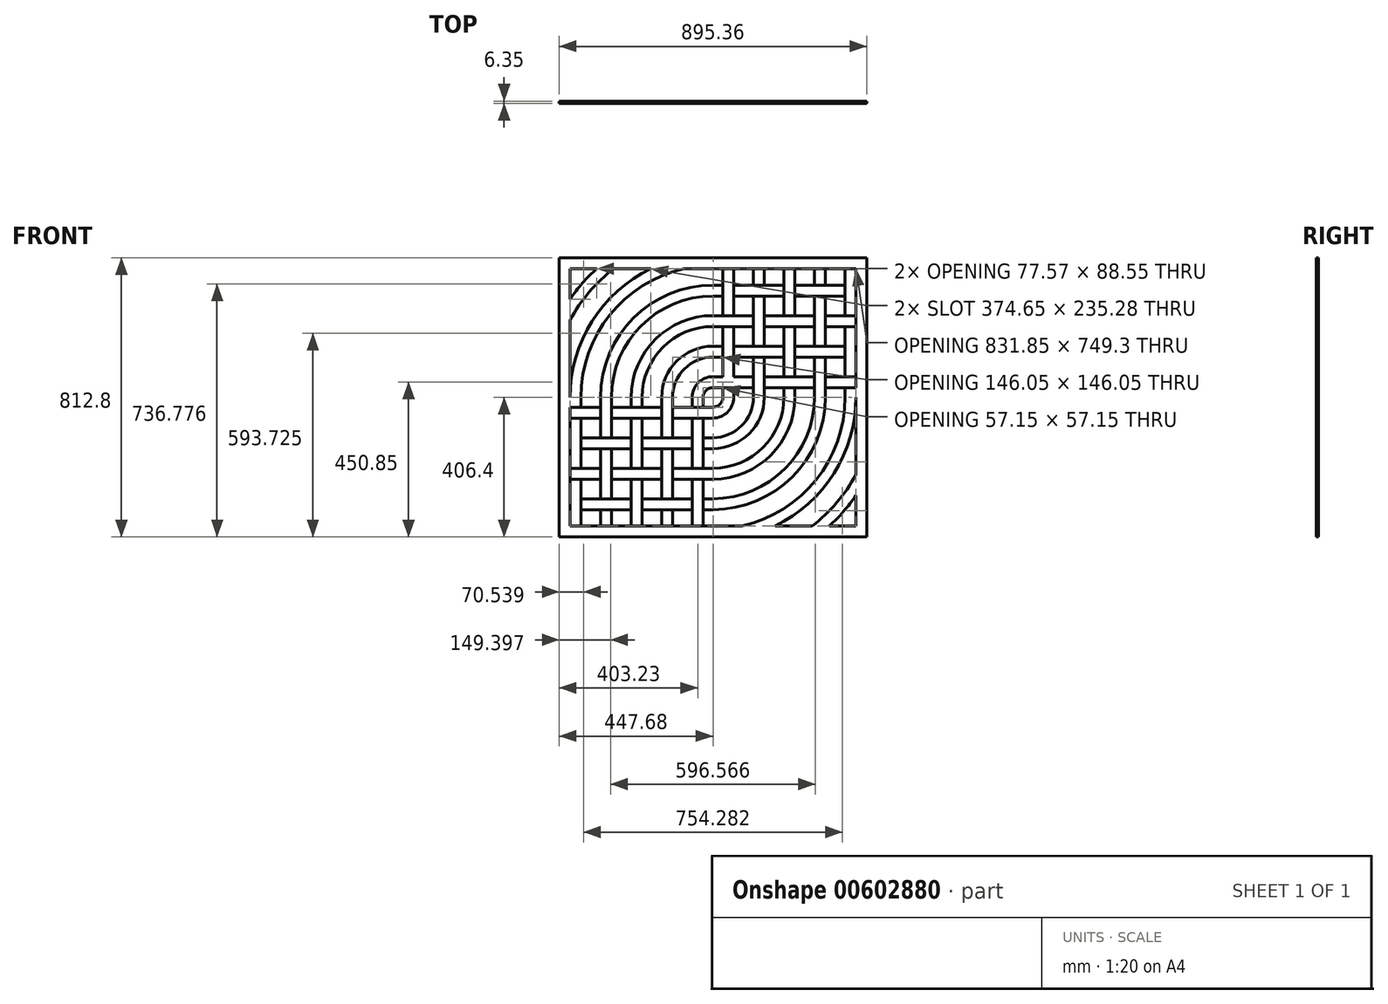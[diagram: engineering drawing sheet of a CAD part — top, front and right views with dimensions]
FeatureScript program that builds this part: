
annotation { "Feature Type Name" : "Feature", "Feature Type Description" : "" }
export const myFeature = defineFeature(function(context is Context, id is Id, definition is map)
    precondition{}
    {
        {
            var Q0;
            Q0=qCreatedBy(makeId("Front.planeOp"),FACE);
            var sketch = newSketch(context, id + "F0", { "sketchPlane" : qUnion([Q0])});
            skLineSegment(sketch, "E0.bottom", {"start": v(447.67, -406.4) * mm, "end": v(-447.68, -406.4) * mm});
            skLineSegment(sketch, "E0.top", {"start": v(447.68, 406.4) * mm, "end": v(-447.68, 406.4) * mm});
            skPoint(sketch, "E0.middle", {"position": v(0, 0) * mm});
            skArc(sketch, "E1", {"start": v(0, 28.58) * mm, "mid": v(-20.2, 20.2) * mm, "end": v(-28.58, 0) * mm});
            skArc(sketch, "E2.0", {"start": v(0, 60.33) * mm, "mid": v(-42.66, 42.66) * mm, "end": v(-60.33, 0) * mm});
            skLineSegment(sketch, "E3.0", {"start": v(415.93, 374.65) * mm, "end": v(-415.92, 374.65) * mm});
            skLineSegment(sketch, "E4.0", {"start": v(415.93, -374.65) * mm, "end": v(-415.93, -374.65) * mm});
            skArc(sketch, "E5.0", {"start": v(0, 117.48) * mm, "mid": v(-83.07, 83.07) * mm, "end": v(-117.48, 0) * mm});
            skArc(sketch, "E6.0", {"start": v(0, 149.22) * mm, "mid": v(-105.52, 105.52) * mm, "end": v(-149.22, 0) * mm});
            skArc(sketch, "E7.0", {"start": v(0, 206.38) * mm, "mid": v(-145.93, 145.93) * mm, "end": v(-206.38, 0) * mm});
            skLineSegment(sketch, "E8", {"start": v(-327.03, 0) * mm, "end": v(-327.03, -117.48) * mm});
            skLineSegment(sketch, "E9.0", {"start": v(-295.28, 0) * mm, "end": v(-295.28, -117.48) * mm});
            skLineSegment(sketch, "E10.0", {"start": v(-238.13, 0) * mm, "end": v(-238.13, -28.58) * mm});
            skLineSegment(sketch, "E11.0", {"start": v(28.57, 0) * mm, "end": v(28.57, 28.57) * mm});
            skLineSegment(sketch, "E12.0", {"start": v(60.32, 0) * mm, "end": v(60.32, 28.57) * mm});
            skLineSegment(sketch, "E13.0", {"start": v(117.47, 0) * mm, "end": v(117.47, 117.48) * mm});
            skLineSegment(sketch, "E14.0", {"start": v(149.22, 0) * mm, "end": v(149.22, 117.48) * mm});
            skLineSegment(sketch, "E15.0", {"start": v(206.37, 0) * mm, "end": v(206.37, 28.58) * mm});
            skLineSegment(sketch, "E16.0", {"start": v(238.12, 0) * mm, "end": v(238.12, 28.58) * mm});
            skLineSegment(sketch, "E17.0", {"start": v(295.27, 0) * mm, "end": v(295.27, 117.48) * mm});
            skLineSegment(sketch, "E18.0", {"start": v(327.02, 0) * mm, "end": v(327.02, 117.48) * mm});
            skLineSegment(sketch, "E19.0", {"start": v(-28.58, 0) * mm, "end": v(-28.58, -28.58) * mm});
            skLineSegment(sketch, "E20.0", {"start": v(-60.33, 0) * mm, "end": v(-60.33, -28.58) * mm});
            skLineSegment(sketch, "E21.0", {"start": v(-117.48, 0) * mm, "end": v(-117.48, -117.48) * mm});
            skLineSegment(sketch, "E22.0", {"start": v(-149.23, 0) * mm, "end": v(-149.23, -117.48) * mm});
            skLineSegment(sketch, "E23.0", {"start": v(-206.38, 0) * mm, "end": v(-206.38, -28.58) * mm});
            skLineSegment(sketch, "E24", {"start": v(0, 28.58) * mm, "end": v(117.47, 28.58) * mm});
            skLineSegment(sketch, "E25", {"start": v(0, 60.33) * mm, "end": v(117.47, 60.33) * mm});
            skLineSegment(sketch, "E26", {"start": v(0, -28.58) * mm, "end": v(-117.48, -28.58) * mm});
            skLineSegment(sketch, "E27", {"start": v(0, -60.33) * mm, "end": v(-117.48, -60.33) * mm});
            skLineSegment(sketch, "E28.0", {"start": v(0, 117.48) * mm, "end": v(28.57, 117.48) * mm});
            skLineSegment(sketch, "E29", {"start": v(0, 149.22) * mm, "end": v(28.57, 149.22) * mm});
            skLineSegment(sketch, "E30", {"start": v(0, 206.38) * mm, "end": v(118.8, 206.38) * mm});
            skLineSegment(sketch, "E31", {"start": v(0, 238.12) * mm, "end": v(117.47, 238.12) * mm});
            skLineSegment(sketch, "E32", {"start": v(0, 295.28) * mm, "end": v(28.57, 295.28) * mm});
            skLineSegment(sketch, "E33", {"start": v(0, 327.03) * mm, "end": v(28.57, 327.03) * mm});
            skArc(sketch, "E34.0", {"start": v(-85.02, 374.65) * mm, "mid": v(-300.2, 239.72) * mm, "end": v(-384.18, 0) * mm});
            skArc(sketch, "E35.0", {"start": v(-288.86, 374.65) * mm, "mid": v(-360.2, 306.68) * mm, "end": v(-415.93, 225.4) * mm});
            skArc(sketch, "E36.0", {"start": v(-338.36, 374.65) * mm, "mid": v(-379.73, 332.64) * mm, "end": v(-415.92, 286.1) * mm});
            skArc(sketch, "E37.trimOffspring", {"start": v(384.58, 327.02) * mm, "mid": v(384.38, 327.26) * mm, "end": v(384.17, 327.5) * mm});
            skArc(sketch, "E38.trimOffspring", {"start": v(338.36, -374.65) * mm, "mid": v(379.73, -332.64) * mm, "end": v(415.93, -286.1) * mm});
            skArc(sketch, "E39.trimOffspring", {"start": v(288.86, -374.65) * mm, "mid": v(360.2, -306.68) * mm, "end": v(415.93, -225.4) * mm});
            skArc(sketch, "E40.trimOffspring", {"start": v(180.64, -374.65) * mm, "mid": v(352.23, -221.2) * mm, "end": v(415.93, 0) * mm});
            skArc(sketch, "E41.trimOffspring", {"start": v(85.02, -374.65) * mm, "mid": v(300.2, -239.72) * mm, "end": v(384.18, 0) * mm});
            skLineSegment(sketch, "E42", {"start": v(-415.93, 0) * mm, "end": v(-415.93, 374.65) * mm});
            skLineSegment(sketch, "E43", {"start": v(-415.93, 0) * mm, "end": v(-415.93, -374.65) * mm});
            skLineSegment(sketch, "E44", {"start": v(415.93, 0) * mm, "end": v(415.93, 374.65) * mm});
            skLineSegment(sketch, "E45", {"start": v(415.93, 0) * mm, "end": v(415.93, -374.65) * mm});
            skLineSegment(sketch, "E46.0", {"start": v(-447.68, 0) * mm, "end": v(-447.68, 406.4) * mm});
            skLineSegment(sketch, "E47.0", {"start": v(447.68, 0) * mm, "end": v(447.68, -406.4) * mm});
            skLineSegment(sketch, "E48.0", {"start": v(447.68, 0) * mm, "end": v(447.68, 406.4) * mm});
            skLineSegment(sketch, "E49", {"start": v(-447.68, 0) * mm, "end": v(-447.68, -406.4) * mm});
            skLineSegment(sketch, "E50", {"start": v(0, -117.48) * mm, "end": v(-28.58, -117.48) * mm});
            skLineSegment(sketch, "E51", {"start": v(0, -149.22) * mm, "end": v(-28.58, -149.22) * mm});
            skLineSegment(sketch, "E52", {"start": v(0, -206.38) * mm, "end": v(-118.8, -206.38) * mm});
            skLineSegment(sketch, "E53", {"start": v(0, -238.12) * mm, "end": v(-117.48, -238.12) * mm});
            skLineSegment(sketch, "E54", {"start": v(0, -295.28) * mm, "end": v(-28.58, -295.28) * mm});
            skLineSegment(sketch, "E55", {"start": v(0, -327.03) * mm, "end": v(-28.58, -327.03) * mm});
            skLineSegment(sketch, "E56.0", {"start": v(384.18, 0) * mm, "end": v(384.18, 28.58) * mm});
            skArc(sketch, "E57.trimOffspring", {"start": v(118.8, 206.38) * mm, "mid": v(118.14, 206.75) * mm, "end": v(117.47, 207.13) * mm});
            skArc(sketch, "E58.trimOffspring", {"start": v(0, 238.12) * mm, "mid": v(-168.38, 168.38) * mm, "end": v(-238.12, 0) * mm});
            skPoint(sketch, "E59.orphan", {"position": v(0, 238.12) * mm});
            skPoint(sketch, "E60.orphan", {"position": v(0, 206.38) * mm});
            skArc(sketch, "E61.trimOffspring", {"start": v(0, 295.28) * mm, "mid": v(-208.8, 208.8) * mm, "end": v(-295.28, 0) * mm});
            skArc(sketch, "E62.trimOffspring", {"start": v(0, 327.03) * mm, "mid": v(-231.24, 231.24) * mm, "end": v(-327.03, 0) * mm});
            skLineSegment(sketch, "E63.0", {"start": v(-384.18, 0) * mm, "end": v(-384.18, -28.58) * mm});
            skArc(sketch, "E64.trimOffspring", {"start": v(0, -28.58) * mm, "mid": v(20.2, -20.2) * mm, "end": v(28.58, 0) * mm});
            skArc(sketch, "E65.trimOffspring", {"start": v(0, -60.33) * mm, "mid": v(42.66, -42.66) * mm, "end": v(60.33, 0) * mm});
            skArc(sketch, "E66.trimOffspring", {"start": v(0, -117.48) * mm, "mid": v(83.07, -83.07) * mm, "end": v(117.48, 0) * mm});
            skArc(sketch, "E67.trimOffspring", {"start": v(0, -149.22) * mm, "mid": v(105.52, -105.52) * mm, "end": v(149.22, 0) * mm});
            skArc(sketch, "E68.trimOffspring", {"start": v(0, -206.38) * mm, "mid": v(145.93, -145.93) * mm, "end": v(206.38, 0) * mm});
            skArc(sketch, "E69.trimOffspring", {"start": v(0, -238.12) * mm, "mid": v(168.38, -168.38) * mm, "end": v(238.12, 0) * mm});
            skArc(sketch, "E70.trimOffspring", {"start": v(0, -295.28) * mm, "mid": v(208.8, -208.8) * mm, "end": v(295.28, 0) * mm});
            skArc(sketch, "E71.trimOffspring", {"start": v(0, -327.03) * mm, "mid": v(231.24, -231.24) * mm, "end": v(327.03, 0) * mm});
            skArc(sketch, "E72.trimOffspring", {"start": v(-118.8, -206.38) * mm, "mid": v(-118.14, -206.75) * mm, "end": v(-117.48, -207.13) * mm});
            skLineSegment(sketch, "E73.trimOffspring", {"start": v(-117.48, -207.13) * mm, "end": v(-117.48, -295.28) * mm});
            skArc(sketch, "E74.trimOffspring", {"start": v(-384.58, -327.03) * mm, "mid": v(-384.38, -327.26) * mm, "end": v(-384.18, -327.5) * mm});
            skArc(sketch, "E75.0", {"start": v(-180.64, 374.65) * mm, "mid": v(-352.23, 221.2) * mm, "end": v(-415.93, 0) * mm});
            skLineSegment(sketch, "E76.trimOffspring", {"start": v(28.57, 60.33) * mm, "end": v(28.57, 206.38) * mm});
            skLineSegment(sketch, "E77.trimOffspring", {"start": v(60.32, 60.33) * mm, "end": v(60.32, 206.38) * mm});
            skLineSegment(sketch, "E78.trimOffspring", {"start": v(149.22, 60.33) * mm, "end": v(295.27, 60.33) * mm});
            skLineSegment(sketch, "E79.trimOffspring", {"start": v(149.22, 28.58) * mm, "end": v(295.27, 28.58) * mm});
            skLineSegment(sketch, "E80.trimOffspring", {"start": v(206.37, 60.33) * mm, "end": v(206.37, 206.38) * mm});
            skLineSegment(sketch, "E81.trimOffspring", {"start": v(238.12, 60.33) * mm, "end": v(238.12, 206.38) * mm});
            skLineSegment(sketch, "E82.trimOffspring", {"start": v(327.02, 28.58) * mm, "end": v(415.93, 28.58) * mm});
            skLineSegment(sketch, "E83.trimOffspring", {"start": v(327.02, 60.33) * mm, "end": v(415.93, 60.33) * mm});
            skLineSegment(sketch, "E84.trimOffspring", {"start": v(384.18, 60.33) * mm, "end": v(384.18, 206.38) * mm});
            skLineSegment(sketch, "E85.trimOffspring", {"start": v(327.02, 149.22) * mm, "end": v(327.02, 295.28) * mm});
            skLineSegment(sketch, "E86.trimOffspring", {"start": v(295.27, 149.22) * mm, "end": v(295.27, 295.28) * mm});
            skLineSegment(sketch, "E87.trimOffspring", {"start": v(117.47, 149.22) * mm, "end": v(117.47, 295.28) * mm});
            skLineSegment(sketch, "E88.trimOffspring", {"start": v(149.22, 149.22) * mm, "end": v(149.22, 295.28) * mm});
            skLineSegment(sketch, "E89.trimOffspring", {"start": v(238.12, 149.22) * mm, "end": v(384.18, 149.22) * mm});
            skLineSegment(sketch, "E90.trimOffspring", {"start": v(238.12, 117.48) * mm, "end": v(384.18, 117.48) * mm});
            skLineSegment(sketch, "E91.trimOffspring", {"start": v(60.32, 117.48) * mm, "end": v(206.37, 117.48) * mm});
            skLineSegment(sketch, "E92.trimOffspring", {"start": v(60.32, 149.22) * mm, "end": v(206.37, 149.22) * mm});
            skLineSegment(sketch, "E93.trimOffspring", {"start": v(28.57, 238.12) * mm, "end": v(28.57, 374.65) * mm});
            skLineSegment(sketch, "E94.trimOffspring", {"start": v(60.32, 238.12) * mm, "end": v(60.32, 374.65) * mm});
            skLineSegment(sketch, "E95.trimOffspring", {"start": v(149.22, 238.12) * mm, "end": v(295.27, 238.12) * mm});
            skLineSegment(sketch, "E96.trimOffspring", {"start": v(149.22, 206.38) * mm, "end": v(295.27, 206.38) * mm});
            skLineSegment(sketch, "E97.trimOffspring", {"start": v(206.37, 238.12) * mm, "end": v(206.37, 374.65) * mm});
            skLineSegment(sketch, "E98.trimOffspring", {"start": v(238.12, 238.12) * mm, "end": v(238.12, 374.65) * mm});
            skLineSegment(sketch, "E99.trimOffspring", {"start": v(327.02, 238.12) * mm, "end": v(415.93, 238.12) * mm});
            skLineSegment(sketch, "E100.trimOffspring", {"start": v(327.02, 206.38) * mm, "end": v(415.93, 206.38) * mm});
            skLineSegment(sketch, "E101.trimOffspring", {"start": v(384.18, 238.12) * mm, "end": v(384.18, 374.65) * mm});
            skLineSegment(sketch, "E102.trimOffspring", {"start": v(327.02, 327.03) * mm, "end": v(327.02, 374.65) * mm});
            skLineSegment(sketch, "E103.trimOffspring", {"start": v(295.27, 327.03) * mm, "end": v(295.27, 374.65) * mm});
            skLineSegment(sketch, "E104.trimOffspring", {"start": v(238.12, 327.03) * mm, "end": v(384.58, 327.03) * mm});
            skLineSegment(sketch, "E105.trimOffspring", {"start": v(238.12, 295.28) * mm, "end": v(384.18, 295.28) * mm});
            skLineSegment(sketch, "E106.trimOffspring", {"start": v(149.22, 327.03) * mm, "end": v(149.22, 374.65) * mm});
            skLineSegment(sketch, "E107.trimOffspring", {"start": v(117.47, 327.03) * mm, "end": v(117.47, 374.65) * mm});
            skLineSegment(sketch, "E108.trimOffspring", {"start": v(60.32, 327.03) * mm, "end": v(206.37, 327.03) * mm});
            skLineSegment(sketch, "E109.trimOffspring", {"start": v(60.32, 295.28) * mm, "end": v(206.37, 295.28) * mm});
            skLineSegment(sketch, "E110.trimOffspring", {"start": v(-149.23, -28.58) * mm, "end": v(-295.28, -28.58) * mm});
            skLineSegment(sketch, "E111.trimOffspring", {"start": v(-149.23, -60.33) * mm, "end": v(-295.28, -60.33) * mm});
            skLineSegment(sketch, "E112.trimOffspring", {"start": v(-60.33, -60.32) * mm, "end": v(-60.33, -206.38) * mm});
            skLineSegment(sketch, "E113.trimOffspring", {"start": v(-28.58, -60.32) * mm, "end": v(-28.58, -206.38) * mm});
            skLineSegment(sketch, "E114.trimOffspring", {"start": v(-60.33, -117.48) * mm, "end": v(-206.38, -117.48) * mm});
            skLineSegment(sketch, "E115.trimOffspring", {"start": v(-60.33, -149.22) * mm, "end": v(-206.38, -149.22) * mm});
            skLineSegment(sketch, "E116.trimOffspring", {"start": v(-117.48, -149.22) * mm, "end": v(-117.48, -206.38) * mm});
            skLineSegment(sketch, "E117.trimOffspring", {"start": v(-149.23, -149.22) * mm, "end": v(-149.23, -295.28) * mm});
            skLineSegment(sketch, "E118.trimOffspring", {"start": v(-149.23, -206.38) * mm, "end": v(-295.28, -206.38) * mm});
            skLineSegment(sketch, "E119.trimOffspring", {"start": v(-149.23, -238.12) * mm, "end": v(-295.28, -238.12) * mm});
            skLineSegment(sketch, "E120.trimOffspring", {"start": v(-60.33, -238.12) * mm, "end": v(-60.33, -374.65) * mm});
            skLineSegment(sketch, "E121.trimOffspring", {"start": v(-28.58, -238.12) * mm, "end": v(-28.58, -374.65) * mm});
            skLineSegment(sketch, "E122.trimOffspring", {"start": v(-60.33, -295.28) * mm, "end": v(-206.38, -295.28) * mm});
            skLineSegment(sketch, "E123.trimOffspring", {"start": v(-60.33, -327.03) * mm, "end": v(-206.38, -327.03) * mm});
            skLineSegment(sketch, "E124.trimOffspring", {"start": v(-117.48, -327.03) * mm, "end": v(-117.48, -374.65) * mm});
            skLineSegment(sketch, "E125.trimOffspring", {"start": v(-149.23, -327.03) * mm, "end": v(-149.23, -374.65) * mm});
            skLineSegment(sketch, "E126.trimOffspring", {"start": v(-238.12, -327.03) * mm, "end": v(-384.58, -327.03) * mm});
            skLineSegment(sketch, "E127.trimOffspring", {"start": v(-238.12, -295.28) * mm, "end": v(-384.18, -295.28) * mm});
            skLineSegment(sketch, "E128.trimOffspring", {"start": v(-206.38, -238.12) * mm, "end": v(-206.38, -374.65) * mm});
            skLineSegment(sketch, "E129.trimOffspring", {"start": v(-238.12, -238.12) * mm, "end": v(-238.12, -374.65) * mm});
            skLineSegment(sketch, "E130.trimOffspring", {"start": v(-238.12, -149.22) * mm, "end": v(-384.18, -149.22) * mm});
            skLineSegment(sketch, "E131.trimOffspring", {"start": v(-238.12, -117.48) * mm, "end": v(-384.18, -117.48) * mm});
            skLineSegment(sketch, "E132.trimOffspring", {"start": v(-206.38, -60.32) * mm, "end": v(-206.38, -206.38) * mm});
            skLineSegment(sketch, "E133.trimOffspring", {"start": v(-238.13, -60.32) * mm, "end": v(-238.12, -206.38) * mm});
            skLineSegment(sketch, "E134.trimOffspring", {"start": v(-327.03, -60.33) * mm, "end": v(-419.1, -60.33) * mm});
            skLineSegment(sketch, "E135.trimOffspring", {"start": v(-327.03, -28.58) * mm, "end": v(-419.1, -28.58) * mm});
            skLineSegment(sketch, "E136.trimOffspring", {"start": v(-384.18, -60.33) * mm, "end": v(-384.18, -206.38) * mm});
            skPoint(sketch, "E137.orphan", {"position": v(-415.93, -117.48) * mm});
            skPoint(sketch, "E138.orphan", {"position": v(-415.93, -149.22) * mm});
            skLineSegment(sketch, "E139.trimOffspring", {"start": v(-327.03, -149.22) * mm, "end": v(-327.03, -295.28) * mm});
            skLineSegment(sketch, "E140.trimOffspring", {"start": v(-295.28, -149.22) * mm, "end": v(-295.28, -295.28) * mm});
            skLineSegment(sketch, "E141.trimOffspring", {"start": v(-327.03, -206.38) * mm, "end": v(-415.93, -206.38) * mm});
            skLineSegment(sketch, "E142.trimOffspring", {"start": v(-327.03, -238.12) * mm, "end": v(-415.93, -238.12) * mm});
            skLineSegment(sketch, "E143.trimOffspring", {"start": v(-384.18, -238.12) * mm, "end": v(-384.18, -374.65) * mm});
            skLineSegment(sketch, "E144.trimOffspring", {"start": v(-295.28, -327.03) * mm, "end": v(-295.28, -374.65) * mm});
            skLineSegment(sketch, "E145.trimOffspring", {"start": v(-327.03, -327.03) * mm, "end": v(-327.03, -374.65) * mm});
            skSolve(sketch);
        }
        {
            var Q0;
            Q0=makeQuery(id+"F0.imprint","IMPRINT",FACE,{"disambiguationData":[TD([[makeQuery(id+"F0.imprint","IMPRINT",EDGE,{"derivedFrom":sQuery(id+"F0.wireOp",EDGE,"E0.bottom")}),-1.0]])]});
            extrude(context, id + "F1", {"entities" : qUnion([Q0]), "depth" : 6.35 * mm, "offsetDistance" : 25.4 * mm});
        }
        {
            var Q0;
            {var subQ0=sQuery(id+"F0.wireOp",EDGE,"E35.0");Q0=makeQuery(id+"F0.imprint","IMPRINT",FACE,{"disambiguationData":[TD([[makeQuery(id+"F0.imprint","IMPRINT",EDGE,{"derivedFrom":subQ0}),-1.0]])]});}
            var Q1;
            {var subQ4=sQuery(id+"F0.wireOp",EDGE,"E34.0");Q1=makeQuery(id+"F0.imprint","IMPRINT",FACE,{"disambiguationData":[TD([[makeQuery(id+"F0.imprint","IMPRINT",EDGE,{"derivedFrom":subQ4}),-1.0]])]});}
            var Q2;
            {var subQ7=sQuery(id+"F0.wireOp",EDGE,"E32");Q2=makeQuery(id+"F0.imprint","IMPRINT",FACE,{"disambiguationData":[TD([[makeQuery(id+"F0.imprint","IMPRINT",EDGE,{"derivedFrom":subQ7}),1.0]])]});}
            var Q3;
            {var subQ11=sQuery(id+"F0.wireOp",EDGE,"E7.0");Q3=makeQuery(id+"F0.imprint","IMPRINT",FACE,{"disambiguationData":[TD([[makeQuery(id+"F0.imprint","IMPRINT",EDGE,{"derivedFrom":subQ11}),-1.0]])]});}
            var Q4;
            {var subQ12=sQuery(id+"F0.wireOp",EDGE,"E5.0");Q4=makeQuery(id+"F0.imprint","IMPRINT",FACE,{"disambiguationData":[TD([[makeQuery(id+"F0.imprint","IMPRINT",EDGE,{"derivedFrom":subQ12}),-1.0]])]});}
            var Q5;
            {var subQ3=sQuery(id+"F0.wireOp",EDGE,"E1");Q5=makeQuery(id+"F0.imprint","IMPRINT",FACE,{"disambiguationData":[TD([[makeQuery(id+"F0.imprint","IMPRINT",EDGE,{"derivedFrom":subQ3}),-1.0]])]});}
            var Q6;
            {var subQ10=sQuery(id+"F0.wireOp",EDGE,"E11.0");Q6=makeQuery(id+"F0.imprint","IMPRINT",FACE,{"disambiguationData":[TD([[makeQuery(id+"F0.imprint","IMPRINT",EDGE,{"derivedFrom":subQ10}),-1.0]])]});}
            var Q7;
            {var subQ6=sQuery(id+"F0.wireOp",EDGE,"E50");Q7=makeQuery(id+"F0.imprint","IMPRINT",FACE,{"disambiguationData":[TD([[makeQuery(id+"F0.imprint","IMPRINT",EDGE,{"derivedFrom":subQ6}),1.0]])]});}
            var Q8;
            {var subQ10=sQuery(id+"F0.wireOp",EDGE,"E15.0");Q8=makeQuery(id+"F0.imprint","IMPRINT",FACE,{"disambiguationData":[TD([[makeQuery(id+"F0.imprint","IMPRINT",EDGE,{"derivedFrom":subQ10}),-1.0]])]});}
            var Q9;
            {var subQ1=sQuery(id+"F0.wireOp",EDGE,"E54");Q9=makeQuery(id+"F0.imprint","IMPRINT",FACE,{"disambiguationData":[TD([[makeQuery(id+"F0.imprint","IMPRINT",EDGE,{"derivedFrom":subQ1}),1.0]])]});}
            var Q10;
            {var subQ2=sQuery(id+"F0.wireOp",EDGE,"E40.trimOffspring");Q10=makeQuery(id+"F0.imprint","IMPRINT",FACE,{"disambiguationData":[TD([[makeQuery(id+"F0.imprint","IMPRINT",EDGE,{"derivedFrom":subQ2}),1.0]])]});}
            var Q11;
            {var subQ0=sQuery(id+"F0.wireOp",EDGE,"E38.trimOffspring");Q11=makeQuery(id+"F0.imprint","IMPRINT",FACE,{"disambiguationData":[TD([[makeQuery(id+"F0.imprint","IMPRINT",EDGE,{"derivedFrom":subQ0}),1.0]])]});}
            extrude(context, id + "F2", {"entities" : qUnion([Q0, Q1, Q2, Q3, Q4, Q5, Q6, Q7, Q8, Q9, Q10, Q11]), "operationType" : NewBodyOperationType.ADD, "depth" : 6.35 * mm, "offsetDistance" : 25.4 * mm});
        }
        {
            var Q0;
            {var subQ0=sQuery(id+"F0.wireOp",EDGE,"E134.trimOffspring");var subQ4=sQuery(id+"F0.wireOp",EDGE,"E8");var subQ5=makeQuery(id+"F0.imprint","INTERSECT",VERTEX,{"derivedFrom":[subQ4,subQ0]});Q0=makeQuery(id+"F0.imprint","IMPRINT",FACE,{"disambiguationData":[TD([[makeQuery(id+"F0.imprint","IMPRINT",EDGE,{"disambiguationData":[TD([[subQ5,1.0]])],"derivedFrom":subQ4}),-1.0]])]});}
            var Q1;
            {var subQ0=sQuery(id+"F0.wireOp",EDGE,"E110.trimOffspring");var subQ7=sQuery(id+"F0.wireOp",EDGE,"E9.0");var subQ8=makeQuery(id+"F0.imprint","INTERSECT",VERTEX,{"derivedFrom":[subQ7,subQ0]});Q1=makeQuery(id+"F0.imprint","IMPRINT",FACE,{"disambiguationData":[TD([[makeQuery(id+"F0.imprint","IMPRINT",EDGE,{"disambiguationData":[TD([[subQ8,-1.0]])],"derivedFrom":subQ7}),1.0]])]});}
            var Q2;
            {var subQ2=sQuery(id+"F0.wireOp",EDGE,"E133.trimOffspring");var subQ5=sQuery(id+"F0.wireOp",EDGE,"E130.trimOffspring");var subQ9=makeQuery(id+"F0.imprint","INTERSECT",VERTEX,{"derivedFrom":[subQ5,subQ2]});Q2=makeQuery(id+"F0.imprint","IMPRINT",FACE,{"disambiguationData":[TD([[makeQuery(id+"F0.imprint","IMPRINT",EDGE,{"disambiguationData":[TD([[subQ9,-1.0]])],"derivedFrom":subQ5}),-1.0]])]});}
            var Q3;
            {var subQ0=sQuery(id+"F0.wireOp",EDGE,"E114.trimOffspring");var subQ5=sQuery(id+"F0.wireOp",EDGE,"E112.trimOffspring");var subQ6=makeQuery(id+"F0.imprint","INTERSECT",VERTEX,{"derivedFrom":[subQ5,subQ0]});Q3=makeQuery(id+"F0.imprint","IMPRINT",FACE,{"disambiguationData":[TD([[makeQuery(id+"F0.imprint","IMPRINT",EDGE,{"disambiguationData":[TD([[subQ6,-1.0]])],"derivedFrom":subQ5}),-1.0]])]});}
            var Q4;
            {var subQ0=sQuery(id+"F0.wireOp",EDGE,"E141.trimOffspring");var subQ2=sQuery(id+"F0.wireOp",EDGE,"E43");var subQ3=makeQuery(id+"F0.imprint","INTERSECT",VERTEX,{"derivedFrom":[subQ2,subQ0]});Q4=makeQuery(id+"F0.imprint","IMPRINT",FACE,{"disambiguationData":[TD([[makeQuery(id+"F0.imprint","IMPRINT",EDGE,{"disambiguationData":[TD([[subQ3,-1.0]])],"derivedFrom":subQ2}),1.0]])]});}
            var Q5;
            {var subQ1=sQuery(id+"F0.wireOp",EDGE,"E118.trimOffspring");var subQ7=sQuery(id+"F0.wireOp",EDGE,"E117.trimOffspring");var subQ8=makeQuery(id+"F0.imprint","INTERSECT",VERTEX,{"derivedFrom":[subQ7,subQ1]});Q5=makeQuery(id+"F0.imprint","IMPRINT",FACE,{"disambiguationData":[TD([[makeQuery(id+"F0.imprint","IMPRINT",EDGE,{"disambiguationData":[TD([[subQ8,-1.0]])],"derivedFrom":subQ7}),-1.0]])]});}
            var Q6;
            {var subQ0=sQuery(id+"F0.wireOp",EDGE,"E129.trimOffspring");var subQ4=sQuery(id+"F0.wireOp",EDGE,"E126.trimOffspring");var subQ9=makeQuery(id+"F0.imprint","INTERSECT",VERTEX,{"derivedFrom":[subQ4,subQ0]});Q6=makeQuery(id+"F0.imprint","IMPRINT",FACE,{"disambiguationData":[TD([[makeQuery(id+"F0.imprint","IMPRINT",EDGE,{"disambiguationData":[TD([[subQ9,-1.0]])],"derivedFrom":subQ4}),-1.0]])]});}
            var Q7;
            {var subQ0=sQuery(id+"F0.wireOp",EDGE,"E122.trimOffspring");var subQ5=sQuery(id+"F0.wireOp",EDGE,"E120.trimOffspring");var subQ6=makeQuery(id+"F0.imprint","INTERSECT",VERTEX,{"derivedFrom":[subQ5,subQ0]});Q7=makeQuery(id+"F0.imprint","IMPRINT",FACE,{"disambiguationData":[TD([[makeQuery(id+"F0.imprint","IMPRINT",EDGE,{"disambiguationData":[TD([[subQ6,-1.0]])],"derivedFrom":subQ5}),-1.0]])]});}
            extrude(context, id + "F3", {"entities" : qUnion([Q0, Q1, Q2, Q3, Q4, Q5, Q6, Q7]), "depth" : 6.35 * mm, "offsetDistance" : 25.4 * mm});
        }
        {
            var Q0;
            {var subQ4=sQuery(id+"F0.wireOp",EDGE,"E141.trimOffspring");var subQ5=sQuery(id+"F0.wireOp",EDGE,"E43");var subQ6=makeQuery(id+"F0.imprint","INTERSECT",VERTEX,{"derivedFrom":[subQ5,subQ4]});Q0=makeQuery(id+"F0.imprint","IMPRINT",FACE,{"disambiguationData":[TD([[makeQuery(id+"F0.imprint","IMPRINT",EDGE,{"disambiguationData":[TD([[subQ6,1.0]])],"derivedFrom":subQ5}),1.0]])]});}
            var Q1;
            {var subQ0=sQuery(id+"F0.wireOp",EDGE,"E139.trimOffspring");var subQ9=sQuery(id+"F0.wireOp",EDGE,"E127.trimOffspring");var subQ10=makeQuery(id+"F0.imprint","INTERSECT",VERTEX,{"derivedFrom":[subQ9,subQ0]});Q1=makeQuery(id+"F0.imprint","IMPRINT",FACE,{"disambiguationData":[TD([[makeQuery(id+"F0.imprint","IMPRINT",EDGE,{"disambiguationData":[TD([[subQ10,1.0]])],"derivedFrom":subQ9}),-1.0]])]});}
            var Q2;
            {var subQ0=sQuery(id+"F0.wireOp",EDGE,"E132.trimOffspring");var subQ3=sQuery(id+"F0.wireOp",EDGE,"E111.trimOffspring");var subQ4=makeQuery(id+"F0.imprint","INTERSECT",VERTEX,{"derivedFrom":[subQ3,subQ0]});Q2=makeQuery(id+"F0.imprint","IMPRINT",FACE,{"disambiguationData":[TD([[makeQuery(id+"F0.imprint","IMPRINT",EDGE,{"disambiguationData":[TD([[subQ4,-1.0]])],"derivedFrom":subQ3}),1.0]])]});}
            var Q3;
            {var subQ4=sQuery(id+"F0.wireOp",EDGE,"E72.trimOffspring");Q3=makeQuery(id+"F0.imprint","IMPRINT",FACE,{"disambiguationData":[TD([[makeQuery(id+"F0.imprint","IMPRINT",EDGE,{"derivedFrom":subQ4}),-1.0]])]});}
            var Q4;
            {var subQ0=sQuery(id+"F0.wireOp",EDGE,"E128.trimOffspring");var subQ3=sQuery(id+"F0.wireOp",EDGE,"E4.0");var subQ4=makeQuery(id+"F0.imprint","INTERSECT",VERTEX,{"derivedFrom":[subQ3,subQ0]});Q4=makeQuery(id+"F0.imprint","IMPRINT",FACE,{"disambiguationData":[TD([[makeQuery(id+"F0.imprint","IMPRINT",EDGE,{"disambiguationData":[TD([[subQ4,-1.0]])],"derivedFrom":subQ3}),-1.0]])]});}
            var Q5;
            {var subQ0=sQuery(id+"F0.wireOp",EDGE,"E112.trimOffspring");var subQ7=sQuery(id+"F0.wireOp",EDGE,"E27");var subQ8=makeQuery(id+"F0.imprint","INTERSECT",VERTEX,{"derivedFrom":[subQ7,subQ0]});Q5=makeQuery(id+"F0.imprint","IMPRINT",FACE,{"disambiguationData":[TD([[makeQuery(id+"F0.imprint","IMPRINT",EDGE,{"disambiguationData":[TD([[subQ8,1.0]])],"derivedFrom":subQ7}),1.0]])]});}
            var Q6;
            {var subQ0=sQuery(id+"F0.wireOp",EDGE,"E120.trimOffspring");var subQ7=sQuery(id+"F0.wireOp",EDGE,"E4.0");var subQ8=makeQuery(id+"F0.imprint","INTERSECT",VERTEX,{"derivedFrom":[subQ7,subQ0]});Q6=makeQuery(id+"F0.imprint","IMPRINT",FACE,{"disambiguationData":[TD([[makeQuery(id+"F0.imprint","IMPRINT",EDGE,{"disambiguationData":[TD([[subQ8,1.0]])],"derivedFrom":subQ7}),-1.0]])]});}
            var Q7;
            {var subQ0=sQuery(id+"F0.wireOp",EDGE,"E124.trimOffspring");Q7=makeQuery(id+"F0.imprint","IMPRINT",FACE,{"disambiguationData":[TD([[makeQuery(id+"F0.imprint","IMPRINT",EDGE,{"derivedFrom":subQ0}),-1.0]])]});}
            var Q8;
            {var subQ0=sQuery(id+"F0.wireOp",EDGE,"E144.trimOffspring");Q8=makeQuery(id+"F0.imprint","IMPRINT",FACE,{"disambiguationData":[TD([[makeQuery(id+"F0.imprint","IMPRINT",EDGE,{"derivedFrom":subQ0}),-1.0]])]});}
            var Q9;
            {var subQ9=sQuery(id+"F0.wireOp",EDGE,"E74.trimOffspring");Q9=makeQuery(id+"F0.imprint","IMPRINT",FACE,{"disambiguationData":[TD([[makeQuery(id+"F0.imprint","IMPRINT",EDGE,{"derivedFrom":subQ9}),-1.0]])]});}
            extrude(context, id + "F4", {"entities" : qUnion([Q0, Q1, Q2, Q3, Q4, Q5, Q6, Q7, Q8, Q9]), "depth" : 6.35 * mm, "offsetDistance" : 25.4 * mm});
        }
        {
            var Q0;
            {var subQ0=sQuery(id+"F0.wireOp",EDGE,"E93.trimOffspring");var subQ3=sQuery(id+"F0.wireOp",EDGE,"E3.0");var subQ4=makeQuery(id+"F0.imprint","INTERSECT",VERTEX,{"derivedFrom":[subQ3,subQ0]});Q0=makeQuery(id+"F0.imprint","IMPRINT",FACE,{"disambiguationData":[TD([[makeQuery(id+"F0.imprint","IMPRINT",EDGE,{"disambiguationData":[TD([[subQ4,1.0]])],"derivedFrom":subQ3}),1.0]])]});}
            var Q1;
            {var subQ0=sQuery(id+"F0.wireOp",EDGE,"E106.trimOffspring");Q1=makeQuery(id+"F0.imprint","IMPRINT",FACE,{"disambiguationData":[TD([[makeQuery(id+"F0.imprint","IMPRINT",EDGE,{"derivedFrom":subQ0}),1.0]])]});}
            var Q2;
            {var subQ2=sQuery(id+"F0.wireOp",EDGE,"E57.trimOffspring");Q2=makeQuery(id+"F0.imprint","IMPRINT",FACE,{"disambiguationData":[TD([[makeQuery(id+"F0.imprint","IMPRINT",EDGE,{"derivedFrom":subQ2}),-1.0]])]});}
            var Q3;
            {var subQ0=sQuery(id+"F0.wireOp",EDGE,"E97.trimOffspring");var subQ7=sQuery(id+"F0.wireOp",EDGE,"E3.0");var subQ8=makeQuery(id+"F0.imprint","INTERSECT",VERTEX,{"derivedFrom":[subQ7,subQ0]});Q3=makeQuery(id+"F0.imprint","IMPRINT",FACE,{"disambiguationData":[TD([[makeQuery(id+"F0.imprint","IMPRINT",EDGE,{"disambiguationData":[TD([[subQ8,1.0]])],"derivedFrom":subQ7}),1.0]])]});}
            var Q4;
            {var subQ0=sQuery(id+"F0.wireOp",EDGE,"E102.trimOffspring");Q4=makeQuery(id+"F0.imprint","IMPRINT",FACE,{"disambiguationData":[TD([[makeQuery(id+"F0.imprint","IMPRINT",EDGE,{"derivedFrom":subQ0}),1.0]])]});}
            var Q5;
            {var subQ0=sQuery(id+"F0.wireOp",EDGE,"E89.trimOffspring");var subQ4=sQuery(id+"F0.wireOp",EDGE,"E85.trimOffspring");var subQ5=makeQuery(id+"F0.imprint","INTERSECT",VERTEX,{"derivedFrom":[subQ4,subQ0]});Q5=makeQuery(id+"F0.imprint","IMPRINT",FACE,{"disambiguationData":[TD([[makeQuery(id+"F0.imprint","IMPRINT",EDGE,{"disambiguationData":[TD([[subQ5,-1.0]])],"derivedFrom":subQ4}),1.0]])]});}
            var Q6;
            {var subQ8=sQuery(id+"F0.wireOp",EDGE,"E37.trimOffspring");Q6=makeQuery(id+"F0.imprint","IMPRINT",FACE,{"disambiguationData":[TD([[makeQuery(id+"F0.imprint","IMPRINT",EDGE,{"derivedFrom":subQ8}),-1.0]])]});}
            var Q7;
            {var subQ3=sQuery(id+"F0.wireOp",EDGE,"E83.trimOffspring");var subQ5=sQuery(id+"F0.wireOp",EDGE,"E44");var subQ6=makeQuery(id+"F0.imprint","INTERSECT",VERTEX,{"derivedFrom":[subQ5,subQ3]});Q7=makeQuery(id+"F0.imprint","IMPRINT",FACE,{"disambiguationData":[TD([[makeQuery(id+"F0.imprint","IMPRINT",EDGE,{"disambiguationData":[TD([[subQ6,-1.0]])],"derivedFrom":subQ5}),1.0]])]});}
            var Q8;
            {var subQ1=sQuery(id+"F0.wireOp",EDGE,"E80.trimOffspring");var subQ5=sQuery(id+"F0.wireOp",EDGE,"E78.trimOffspring");var subQ6=makeQuery(id+"F0.imprint","INTERSECT",VERTEX,{"derivedFrom":[subQ5,subQ1]});Q8=makeQuery(id+"F0.imprint","IMPRINT",FACE,{"disambiguationData":[TD([[makeQuery(id+"F0.imprint","IMPRINT",EDGE,{"disambiguationData":[TD([[subQ6,-1.0]])],"derivedFrom":subQ5}),1.0]])]});}
            var Q9;
            {var subQ0=sQuery(id+"F0.wireOp",EDGE,"E76.trimOffspring");var subQ3=sQuery(id+"F0.wireOp",EDGE,"E25");var subQ4=makeQuery(id+"F0.imprint","INTERSECT",VERTEX,{"derivedFrom":[subQ3,subQ0]});Q9=makeQuery(id+"F0.imprint","IMPRINT",FACE,{"disambiguationData":[TD([[makeQuery(id+"F0.imprint","IMPRINT",EDGE,{"disambiguationData":[TD([[subQ4,-1.0]])],"derivedFrom":subQ3}),1.0]])]});}
            extrude(context, id + "F5", {"entities" : qUnion([Q0, Q1, Q2, Q3, Q4, Q5, Q6, Q7, Q8, Q9]), "depth" : 6.35 * mm, "offsetDistance" : 25.4 * mm});
        }
        {
            var Q0;
            {var subQ0=sQuery(id+"F0.wireOp",EDGE,"E108.trimOffspring");var subQ2=sQuery(id+"F0.wireOp",EDGE,"E94.trimOffspring");var subQ3=makeQuery(id+"F0.imprint","INTERSECT",VERTEX,{"derivedFrom":[subQ2,subQ0]});Q0=makeQuery(id+"F0.imprint","IMPRINT",FACE,{"disambiguationData":[TD([[makeQuery(id+"F0.imprint","IMPRINT",EDGE,{"disambiguationData":[TD([[subQ3,1.0]])],"derivedFrom":subQ2}),-1.0]])]});}
            var Q1;
            {var subQ0=sQuery(id+"F0.wireOp",EDGE,"E104.trimOffspring");var subQ3=sQuery(id+"F0.wireOp",EDGE,"E98.trimOffspring");var subQ4=makeQuery(id+"F0.imprint","INTERSECT",VERTEX,{"derivedFrom":[subQ3,subQ0]});Q1=makeQuery(id+"F0.imprint","IMPRINT",FACE,{"disambiguationData":[TD([[makeQuery(id+"F0.imprint","IMPRINT",EDGE,{"disambiguationData":[TD([[subQ4,1.0]])],"derivedFrom":subQ3}),-1.0]])]});}
            var Q2;
            {var subQ0=sQuery(id+"F0.wireOp",EDGE,"E95.trimOffspring");var subQ7=sQuery(id+"F0.wireOp",EDGE,"E86.trimOffspring");var subQ8=makeQuery(id+"F0.imprint","INTERSECT",VERTEX,{"derivedFrom":[subQ7,subQ0]});Q2=makeQuery(id+"F0.imprint","IMPRINT",FACE,{"disambiguationData":[TD([[makeQuery(id+"F0.imprint","IMPRINT",EDGE,{"disambiguationData":[TD([[subQ8,1.0]])],"derivedFrom":subQ7}),1.0]])]});}
            var Q3;
            {var subQ0=sQuery(id+"F0.wireOp",EDGE,"E99.trimOffspring");var subQ1=sQuery(id+"F0.wireOp",EDGE,"E44");var subQ2=makeQuery(id+"F0.imprint","INTERSECT",VERTEX,{"derivedFrom":[subQ1,subQ0]});Q3=makeQuery(id+"F0.imprint","IMPRINT",FACE,{"disambiguationData":[TD([[makeQuery(id+"F0.imprint","IMPRINT",EDGE,{"disambiguationData":[TD([[subQ2,1.0]])],"derivedFrom":subQ1}),1.0]])]});}
            var Q4;
            {var subQ0=sQuery(id+"F0.wireOp",EDGE,"E89.trimOffspring");var subQ3=sQuery(id+"F0.wireOp",EDGE,"E81.trimOffspring");var subQ4=makeQuery(id+"F0.imprint","INTERSECT",VERTEX,{"derivedFrom":[subQ3,subQ0]});Q4=makeQuery(id+"F0.imprint","IMPRINT",FACE,{"disambiguationData":[TD([[makeQuery(id+"F0.imprint","IMPRINT",EDGE,{"disambiguationData":[TD([[subQ4,1.0]])],"derivedFrom":subQ3}),-1.0]])]});}
            var Q5;
            {var subQ0=sQuery(id+"F0.wireOp",EDGE,"E91.trimOffspring");var subQ7=sQuery(id+"F0.wireOp",EDGE,"E77.trimOffspring");var subQ8=makeQuery(id+"F0.imprint","INTERSECT",VERTEX,{"derivedFrom":[subQ7,subQ0]});Q5=makeQuery(id+"F0.imprint","IMPRINT",FACE,{"disambiguationData":[TD([[makeQuery(id+"F0.imprint","IMPRINT",EDGE,{"disambiguationData":[TD([[subQ8,-1.0]])],"derivedFrom":subQ7}),-1.0]])]});}
            var Q6;
            {var subQ0=sQuery(id+"F0.wireOp",EDGE,"E78.trimOffspring");var subQ3=sQuery(id+"F0.wireOp",EDGE,"E14.0");var subQ4=makeQuery(id+"F0.imprint","INTERSECT",VERTEX,{"derivedFrom":[subQ3,subQ0]});Q6=makeQuery(id+"F0.imprint","IMPRINT",FACE,{"disambiguationData":[TD([[makeQuery(id+"F0.imprint","IMPRINT",EDGE,{"disambiguationData":[TD([[subQ4,1.0]])],"derivedFrom":subQ3}),-1.0]])]});}
            var Q7;
            {var subQ0=sQuery(id+"F0.wireOp",EDGE,"E82.trimOffspring");var subQ6=sQuery(id+"F0.wireOp",EDGE,"E18.0");var subQ7=makeQuery(id+"F0.imprint","INTERSECT",VERTEX,{"derivedFrom":[subQ6,subQ0]});Q7=makeQuery(id+"F0.imprint","IMPRINT",FACE,{"disambiguationData":[TD([[makeQuery(id+"F0.imprint","IMPRINT",EDGE,{"disambiguationData":[TD([[subQ7,-1.0]])],"derivedFrom":subQ6}),-1.0]])]});}
            extrude(context, id + "F6", {"entities" : qUnion([Q0, Q1, Q2, Q3, Q4, Q5, Q6, Q7]), "depth" : 6.35 * mm, "offsetDistance" : 25.4 * mm});
        }
        {
            var Q0;
            {var subQ12=sQuery(id+"F0.wireOp",EDGE,"E5.0");Q0=makeQuery(id+"F0.imprint","IMPRINT",FACE,{"disambiguationData":[TD([[makeQuery(id+"F0.imprint","IMPRINT",EDGE,{"derivedFrom":subQ12}),-1.0]])]});}
            extrude(context, id + "F7", {"entities" : qUnion([Q0]), "depth" : 6.35 * mm, "offsetDistance" : 25.4 * mm});
        }
        {
            var Q0;
            {var subQ3=sQuery(id+"F0.wireOp",EDGE,"E1");Q0=makeQuery(id+"F0.imprint","IMPRINT",FACE,{"disambiguationData":[TD([[makeQuery(id+"F0.imprint","IMPRINT",EDGE,{"derivedFrom":subQ3}),-1.0]])]});}
            extrude(context, id + "F8", {"entities" : qUnion([Q0]), "operationType" : NewBodyOperationType.ADD, "depth" : 6.35 * mm, "offsetDistance" : 25.4 * mm});
        }
        {
            var Q0;
            {var subQ10=sQuery(id+"F0.wireOp",EDGE,"E11.0");Q0=makeQuery(id+"F0.imprint","IMPRINT",FACE,{"disambiguationData":[TD([[makeQuery(id+"F0.imprint","IMPRINT",EDGE,{"derivedFrom":subQ10}),-1.0]])]});}
            extrude(context, id + "F9", {"entities" : qUnion([Q0]), "depth" : 6.35 * mm, "offsetDistance" : 25.4 * mm});
        }
        {
            var Q0;
            {var subQ6=sQuery(id+"F0.wireOp",EDGE,"E50");Q0=makeQuery(id+"F0.imprint","IMPRINT",FACE,{"disambiguationData":[TD([[makeQuery(id+"F0.imprint","IMPRINT",EDGE,{"derivedFrom":subQ6}),1.0]])]});}
            extrude(context, id + "F10", {"entities" : qUnion([Q0]), "depth" : 6.35 * mm, "offsetDistance" : 25.4 * mm});
        }
    });
